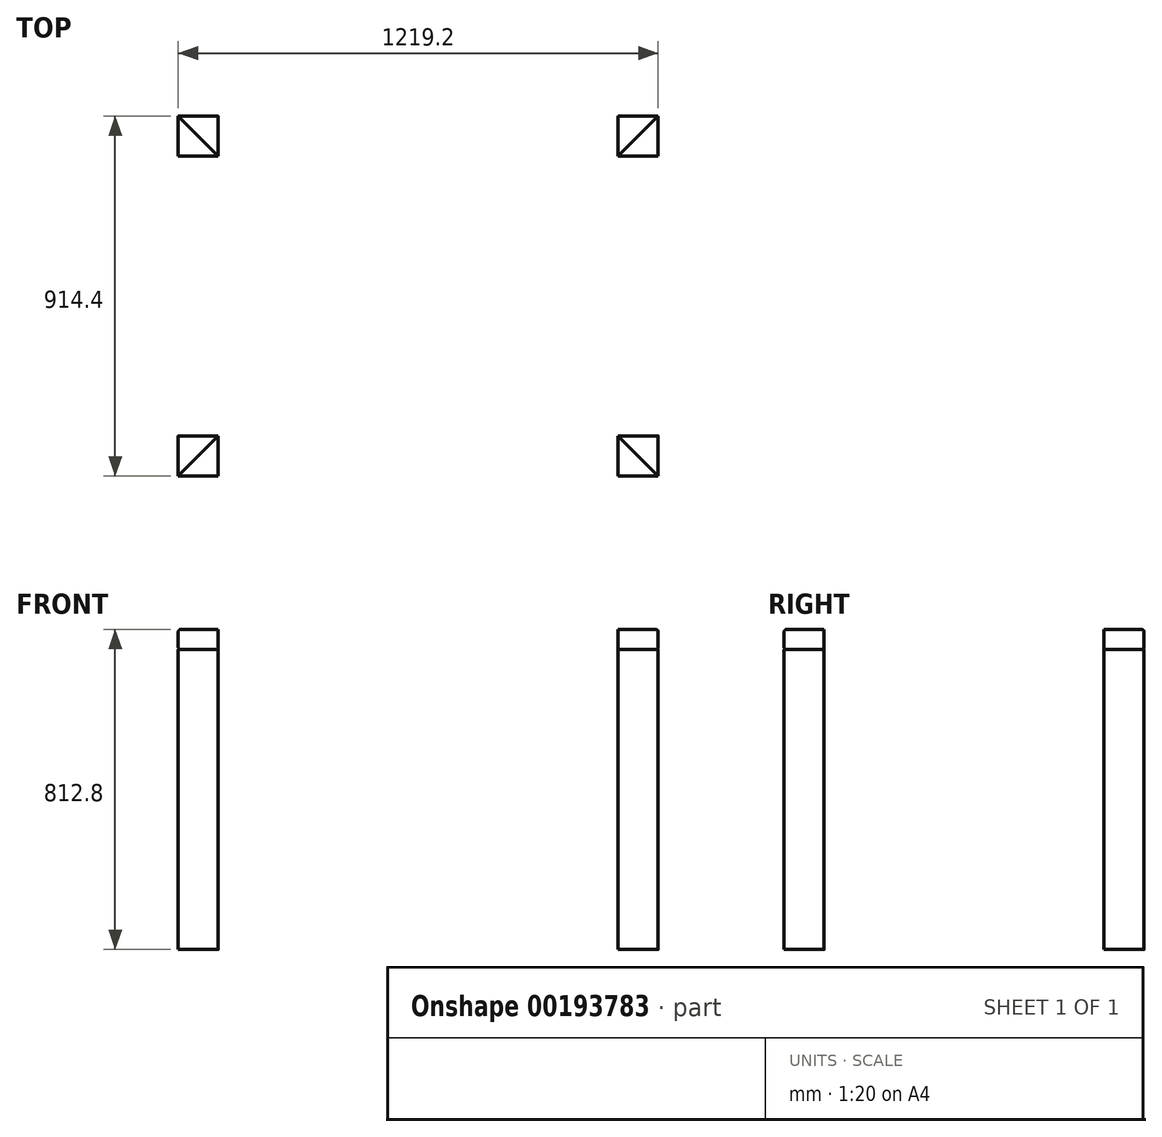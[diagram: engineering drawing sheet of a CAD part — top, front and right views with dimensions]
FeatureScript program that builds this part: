
annotation { "Feature Type Name" : "Feature", "Feature Type Description" : "" }
export const myFeature = defineFeature(function(context is Context, id is Id, definition is map)
    precondition{}
    {
        {
            var Q0;
            Q0=qCreatedBy(makeId("Top.planeOp"),FACE);
            var sketch = newSketch(context, id + "F0", { "sketchPlane" : qUnion([Q0])});
            skLineSegment(sketch, "E0.bottom", {"start": v(-609.6, 457.2) * mm, "end": v(609.6, 457.2) * mm});
            skLineSegment(sketch, "E0.top", {"start": v(-609.6, -457.2) * mm, "end": v(609.6, -457.2) * mm});
            skLineSegment(sketch, "E0.left", {"start": v(-609.6, 457.2) * mm, "end": v(-609.6, -457.2) * mm});
            skLineSegment(sketch, "E0.right", {"start": v(609.6, 457.2) * mm, "end": v(609.6, -457.2) * mm});
            skLineSegment(sketch, "E1.bottom", {"start": v(-508, 355.6) * mm, "end": v(508, 355.6) * mm});
            skLineSegment(sketch, "E1.top", {"start": v(-508, -355.6) * mm, "end": v(508, -355.6) * mm});
            skLineSegment(sketch, "E1.left", {"start": v(-508, 355.6) * mm, "end": v(-508, -355.6) * mm});
            skLineSegment(sketch, "E1.right", {"start": v(508, 355.6) * mm, "end": v(508, -355.6) * mm});
            skLineSegment(sketch, "E2", {"start": v(-609.6, 457.2) * mm, "end": v(-508, 355.6) * mm});
            skLineSegment(sketch, "E3", {"start": v(-609.6, -457.2) * mm, "end": v(-508, -355.6) * mm});
            skLineSegment(sketch, "E4", {"start": v(609.6, -457.2) * mm, "end": v(508, -355.6) * mm});
            skLineSegment(sketch, "E5", {"start": v(609.6, 457.2) * mm, "end": v(508, 355.6) * mm});
            skLineSegment(sketch, "E6.bottom", {"start": v(-609.6, 457.2) * mm, "end": v(-508, 457.2) * mm});
            skLineSegment(sketch, "E6.top", {"start": v(-609.6, 355.6) * mm, "end": v(-508, 355.6) * mm});
            skLineSegment(sketch, "E6.left", {"start": v(-609.6, 457.2) * mm, "end": v(-609.6, 355.6) * mm});
            skLineSegment(sketch, "E6.right", {"start": v(-508, 457.2) * mm, "end": v(-508, 355.6) * mm});
            skLineSegment(sketch, "E7.bottom", {"start": v(-609.6, -457.2) * mm, "end": v(-508, -457.2) * mm});
            skLineSegment(sketch, "E7.top", {"start": v(-609.6, -355.6) * mm, "end": v(-508, -355.6) * mm});
            skLineSegment(sketch, "E7.left", {"start": v(-609.6, -457.2) * mm, "end": v(-609.6, -355.6) * mm});
            skLineSegment(sketch, "E7.right", {"start": v(-508, -457.2) * mm, "end": v(-508, -355.6) * mm});
            skLineSegment(sketch, "E8.bottom", {"start": v(609.6, -457.2) * mm, "end": v(508, -457.2) * mm});
            skLineSegment(sketch, "E8.top", {"start": v(609.6, -355.6) * mm, "end": v(508, -355.6) * mm});
            skLineSegment(sketch, "E8.left", {"start": v(609.6, -457.2) * mm, "end": v(609.6, -355.6) * mm});
            skLineSegment(sketch, "E8.right", {"start": v(508, -457.2) * mm, "end": v(508, -355.6) * mm});
            skLineSegment(sketch, "E9.bottom", {"start": v(-750.07, 827.14) * mm, "end": v(-773.47, 827.14) * mm});
            skLineSegment(sketch, "E9.top", {"start": v(-750.07, 756.94) * mm, "end": v(-773.47, 756.94) * mm});
            skLineSegment(sketch, "E9.left", {"start": v(-750.07, 827.14) * mm, "end": v(-750.07, 756.94) * mm});
            skLineSegment(sketch, "E9.right", {"start": v(-773.47, 827.14) * mm, "end": v(-773.47, 756.94) * mm});
            skLineSegment(sketch, "E10.bottom", {"start": v(609.6, 457.2) * mm, "end": v(508, 457.2) * mm});
            skLineSegment(sketch, "E10.top", {"start": v(609.6, 355.6) * mm, "end": v(508, 355.6) * mm});
            skLineSegment(sketch, "E10.left", {"start": v(609.6, 457.2) * mm, "end": v(609.6, 355.6) * mm});
            skLineSegment(sketch, "E10.right", {"start": v(508, 457.2) * mm, "end": v(508, 355.6) * mm});
            skSolve(sketch);
        }
        {
            var Q0;
            Q0=makeQuery(id+"F0.imprint","IMPRINT",FACE,{"disambiguationData":[TD([[makeQuery(id+"F0.imprint","IMPRINT",EDGE,{"derivedFrom":sQuery(id+"F0.wireOp",EDGE,"E0.left")}),1.0]])]});
            var Q1;
            Q1=makeQuery(id+"F0.imprint","IMPRINT",FACE,{"disambiguationData":[TD([[makeQuery(id+"F0.imprint","IMPRINT",EDGE,{"derivedFrom":sQuery(id+"F0.wireOp",EDGE,"E2")}),-1.0]])]});
            var Q2;
            Q2=makeQuery(id+"F0.imprint","IMPRINT",FACE,{"disambiguationData":[TD([[makeQuery(id+"F0.imprint","IMPRINT",EDGE,{"derivedFrom":sQuery(id+"F0.wireOp",EDGE,"E3")}),1.0]])]});
            extrude(context, id + "F1", {"entities" : qUnion([Q0, Q1, Q2]), "depth" : 50.8 * mm});
        }
        {
            var Q0;
            Q0=makeQuery(id+"F0.imprint","IMPRINT",FACE,{"disambiguationData":[TD([[makeQuery(id+"F0.imprint","IMPRINT",EDGE,{"derivedFrom":sQuery(id+"F0.wireOp",EDGE,"E0.bottom")}),-1.0]])]});
            var Q1;
            Q1=makeQuery(id+"F0.imprint","IMPRINT",FACE,{"disambiguationData":[TD([[makeQuery(id+"F0.imprint","IMPRINT",EDGE,{"derivedFrom":sQuery(id+"F0.wireOp",EDGE,"E2")}),1.0]])]});
            var Q2;
            Q2=makeQuery(id+"F0.imprint","IMPRINT",FACE,{"disambiguationData":[TD([[makeQuery(id+"F0.imprint","IMPRINT",EDGE,{"derivedFrom":sQuery(id+"F0.wireOp",EDGE,"E5")}),-1.0]])]});
            extrude(context, id + "F2", {"entities" : qUnion([Q0, Q1, Q2]), "depth" : 50.8 * mm});
        }
        {
            var Q0;
            Q0=makeQuery(id+"F0.imprint","IMPRINT",FACE,{"disambiguationData":[TD([[makeQuery(id+"F0.imprint","IMPRINT",EDGE,{"derivedFrom":sQuery(id+"F0.wireOp",EDGE,"E0.right")}),-1.0]])]});
            var Q1;
            Q1=makeQuery(id+"F0.imprint","IMPRINT",FACE,{"disambiguationData":[TD([[makeQuery(id+"F0.imprint","IMPRINT",EDGE,{"derivedFrom":sQuery(id+"F0.wireOp",EDGE,"E4")}),-1.0]])]});
            var Q2;
            Q2=makeQuery(id+"F0.imprint","IMPRINT",FACE,{"disambiguationData":[TD([[makeQuery(id+"F0.imprint","IMPRINT",EDGE,{"derivedFrom":sQuery(id+"F0.wireOp",EDGE,"E5")}),1.0]])]});
            extrude(context, id + "F3", {"entities" : qUnion([Q0, Q1, Q2]), "depth" : 50.8 * mm});
        }
        {
            var Q0;
            Q0=makeQuery(id+"F0.imprint","IMPRINT",FACE,{"disambiguationData":[TD([[makeQuery(id+"F0.imprint","IMPRINT",EDGE,{"derivedFrom":sQuery(id+"F0.wireOp",EDGE,"E0.top")}),1.0]])]});
            var Q1;
            Q1=makeQuery(id+"F0.imprint","IMPRINT",FACE,{"disambiguationData":[TD([[makeQuery(id+"F0.imprint","IMPRINT",EDGE,{"derivedFrom":sQuery(id+"F0.wireOp",EDGE,"E4")}),1.0]])]});
            var Q2;
            Q2=makeQuery(id+"F0.imprint","IMPRINT",FACE,{"disambiguationData":[TD([[makeQuery(id+"F0.imprint","IMPRINT",EDGE,{"derivedFrom":sQuery(id+"F0.wireOp",EDGE,"E3")}),-1.0]])]});
            extrude(context, id + "F4", {"entities" : qUnion([Q0, Q1, Q2]), "depth" : 50.8 * mm});
        }
        {
            var Q0;
            Q0=makeQuery(id+"F4.opExtrude","CAP_EDGE",EDGE,{"disambiguationData":[OSD([sQuery(id+"F0.wireOp",EDGE,"E0.top"),sQuery(id+"F0.wireOp",EDGE,"E7.bottom"),sQuery(id+"F0.wireOp",EDGE,"E8.bottom")])],"isStart":false});
            var Q1;
            Q1=makeQuery(id+"F4.opExtrude","CAP_EDGE",EDGE,{"disambiguationData":[OSD([sQuery(id+"F0.wireOp",EDGE,"E0.top"),sQuery(id+"F0.wireOp",EDGE,"E7.bottom"),sQuery(id+"F0.wireOp",EDGE,"E8.bottom")])],"isStart":true});
            var Q2;
            Q2=makeQuery(id+"F4.opExtrude","CAP_EDGE",EDGE,{"disambiguationData":[OSD([sQuery(id+"F0.wireOp",EDGE,"E1.top")])],"isStart":false});
            var Q3;
            Q3=makeQuery(id+"F4.opExtrude","CAP_EDGE",EDGE,{"disambiguationData":[OSD([sQuery(id+"F0.wireOp",EDGE,"E1.top")])],"isStart":true});
            var Q4;
            Q4=makeQuery(id+"F3.opExtrude","CAP_EDGE",EDGE,{"disambiguationData":[OSD([sQuery(id+"F0.wireOp",EDGE,"E0.right"),sQuery(id+"F0.wireOp",EDGE,"E8.left"),sQuery(id+"F0.wireOp",EDGE,"E10.left")])],"isStart":true});
            var Q5;
            Q5=makeQuery(id+"F3.opExtrude","CAP_EDGE",EDGE,{"disambiguationData":[OSD([sQuery(id+"F0.wireOp",EDGE,"E0.right"),sQuery(id+"F0.wireOp",EDGE,"E8.left"),sQuery(id+"F0.wireOp",EDGE,"E10.left")])],"isStart":false});
            var Q6;
            Q6=makeQuery(id+"F3.opExtrude","CAP_EDGE",EDGE,{"disambiguationData":[OSD([sQuery(id+"F0.wireOp",EDGE,"E1.right")])],"isStart":false});
            var Q7;
            Q7=makeQuery(id+"F1.opExtrude","CAP_EDGE",EDGE,{"disambiguationData":[OSD([sQuery(id+"F0.wireOp",EDGE,"E1.left")])],"isStart":true});
            var Q8;
            Q8=makeQuery(id+"F1.opExtrude","CAP_EDGE",EDGE,{"disambiguationData":[OSD([sQuery(id+"F0.wireOp",EDGE,"E1.left")])],"isStart":false});
            var Q9;
            Q9=makeQuery(id+"F1.opExtrude","CAP_EDGE",EDGE,{"disambiguationData":[OSD([sQuery(id+"F0.wireOp",EDGE,"E0.left"),sQuery(id+"F0.wireOp",EDGE,"E6.left"),sQuery(id+"F0.wireOp",EDGE,"E7.left")])],"isStart":false});
            var Q10;
            Q10=makeQuery(id+"F2.opExtrude","CAP_EDGE",EDGE,{"disambiguationData":[OSD([sQuery(id+"F0.wireOp",EDGE,"E1.bottom")])],"isStart":false});
            var Q11;
            Q11=makeQuery(id+"F2.opExtrude","CAP_EDGE",EDGE,{"disambiguationData":[OSD([sQuery(id+"F0.wireOp",EDGE,"E0.bottom"),sQuery(id+"F0.wireOp",EDGE,"E6.bottom"),sQuery(id+"F0.wireOp",EDGE,"E10.bottom")])],"isStart":false});
            var Q12;
            Q12=makeQuery(id+"F2.opExtrude","CAP_EDGE",EDGE,{"disambiguationData":[OSD([sQuery(id+"F0.wireOp",EDGE,"E0.bottom"),sQuery(id+"F0.wireOp",EDGE,"E6.bottom"),sQuery(id+"F0.wireOp",EDGE,"E10.bottom")])],"isStart":true});
            var Q13;
            Q13=makeQuery(id+"F2.opExtrude","CAP_EDGE",EDGE,{"disambiguationData":[OSD([sQuery(id+"F0.wireOp",EDGE,"E1.bottom")])],"isStart":true});
            var Q14;
            Q14=makeQuery(id+"F1.opExtrude","CAP_EDGE",EDGE,{"disambiguationData":[OSD([sQuery(id+"F0.wireOp",EDGE,"E0.left"),sQuery(id+"F0.wireOp",EDGE,"E6.left"),sQuery(id+"F0.wireOp",EDGE,"E7.left")])],"isStart":true});
            var Q15;
            Q15=makeQuery(id+"F3.opExtrude","CAP_EDGE",EDGE,{"disambiguationData":[OSD([sQuery(id+"F0.wireOp",EDGE,"E1.right")])],"isStart":true});
            fillet(context, id + "F5", {"entities" : qUnion([Q0, Q1, Q2, Q3, Q4, Q5, Q6, Q7, Q8, Q9, Q10, Q11, Q12, Q13, Q14, Q15]), "radius" : 6.35 * mm, "tangentPropagation" : true, "allowEdgeOverflow" : false});
        }
        {
            var Q0;
            Q0=makeQuery(id+"F0.imprint","IMPRINT",FACE,{"disambiguationData":[TD([[makeQuery(id+"F0.imprint","IMPRINT",EDGE,{"derivedFrom":sQuery(id+"F0.wireOp",EDGE,"E2")}),1.0]])]});
            var Q1;
            Q1=makeQuery(id+"F0.imprint","IMPRINT",FACE,{"disambiguationData":[TD([[makeQuery(id+"F0.imprint","IMPRINT",EDGE,{"derivedFrom":sQuery(id+"F0.wireOp",EDGE,"E2")}),-1.0]])]});
            extrude(context, id + "F6", {"entities" : qUnion([Q0, Q1]), "oppositeDirection" : true, "depth" : 762 * mm});
        }
        {
            var Q0;
            Q0=makeQuery(id+"F0.imprint","IMPRINT",FACE,{"disambiguationData":[TD([[makeQuery(id+"F0.imprint","IMPRINT",EDGE,{"derivedFrom":sQuery(id+"F0.wireOp",EDGE,"E3")}),1.0]])]});
            var Q1;
            Q1=makeQuery(id+"F0.imprint","IMPRINT",FACE,{"disambiguationData":[TD([[makeQuery(id+"F0.imprint","IMPRINT",EDGE,{"derivedFrom":sQuery(id+"F0.wireOp",EDGE,"E3")}),-1.0]])]});
            extrude(context, id + "F7", {"entities" : qUnion([Q0, Q1]), "oppositeDirection" : true, "depth" : 762 * mm});
        }
        {
            var Q0;
            Q0=makeQuery(id+"F0.imprint","IMPRINT",FACE,{"disambiguationData":[TD([[makeQuery(id+"F0.imprint","IMPRINT",EDGE,{"derivedFrom":sQuery(id+"F0.wireOp",EDGE,"E5")}),1.0]])]});
            var Q1;
            Q1=makeQuery(id+"F0.imprint","IMPRINT",FACE,{"disambiguationData":[TD([[makeQuery(id+"F0.imprint","IMPRINT",EDGE,{"derivedFrom":sQuery(id+"F0.wireOp",EDGE,"E5")}),-1.0]])]});
            extrude(context, id + "F8", {"entities" : qUnion([Q0, Q1]), "oppositeDirection" : true, "depth" : 762 * mm});
        }
        {
            var Q0;
            Q0=makeQuery(id+"F0.imprint","IMPRINT",FACE,{"disambiguationData":[TD([[makeQuery(id+"F0.imprint","IMPRINT",EDGE,{"derivedFrom":sQuery(id+"F0.wireOp",EDGE,"E4")}),1.0]])]});
            var Q1;
            Q1=makeQuery(id+"F0.imprint","IMPRINT",FACE,{"disambiguationData":[TD([[makeQuery(id+"F0.imprint","IMPRINT",EDGE,{"derivedFrom":sQuery(id+"F0.wireOp",EDGE,"E4")}),-1.0]])]});
            extrude(context, id + "F9", {"entities" : qUnion([Q0, Q1]), "oppositeDirection" : true, "depth" : 762 * mm});
        }
        {
            var Q0;
            Q0=makeQuery(id+"F9.opExtrude","SWEPT_EDGE",EDGE,{"disambiguationData":[OSD([sQuery(id+"F0.wireOp",EDGE,"E4"),sQuery(id+"F0.wireOp",EDGE,"E8.bottom"),sQuery(id+"F0.wireOp",EDGE,"E8.left")])]});
            var Q1;
            Q1=makeQuery(id+"F9.opExtrude","SWEPT_EDGE",EDGE,{"disambiguationData":[OSD([sQuery(id+"F0.wireOp",EDGE,"E0.top"),sQuery(id+"F0.wireOp",EDGE,"E8.bottom"),sQuery(id+"F0.wireOp",EDGE,"E8.right")])]});
            var Q2;
            Q2=makeQuery(id+"F9.opExtrude","SWEPT_EDGE",EDGE,{"disambiguationData":[OSD([sQuery(id+"F0.wireOp",EDGE,"E0.right"),sQuery(id+"F0.wireOp",EDGE,"E8.top"),sQuery(id+"F0.wireOp",EDGE,"E8.left")])]});
            var Q3;
            Q3=makeQuery(id+"F7.opExtrude","SWEPT_EDGE",EDGE,{"disambiguationData":[OSD([sQuery(id+"F0.wireOp",EDGE,"E1.top"),sQuery(id+"F0.wireOp",EDGE,"E1.left"),sQuery(id+"F0.wireOp",EDGE,"E3"),sQuery(id+"F0.wireOp",EDGE,"E7.top"),sQuery(id+"F0.wireOp",EDGE,"E7.right")])]});
            var Q4;
            Q4=makeQuery(id+"F7.opExtrude","SWEPT_EDGE",EDGE,{"disambiguationData":[OSD([sQuery(id+"F0.wireOp",EDGE,"E0.top"),sQuery(id+"F0.wireOp",EDGE,"E7.bottom"),sQuery(id+"F0.wireOp",EDGE,"E7.right")])]});
            var Q5;
            Q5=makeQuery(id+"F7.opExtrude","SWEPT_EDGE",EDGE,{"disambiguationData":[OSD([sQuery(id+"F0.wireOp",EDGE,"E3"),sQuery(id+"F0.wireOp",EDGE,"E7.bottom"),sQuery(id+"F0.wireOp",EDGE,"E7.left")])]});
            var Q6;
            Q6=makeQuery(id+"F6.opExtrude","SWEPT_EDGE",EDGE,{"disambiguationData":[OSD([sQuery(id+"F0.wireOp",EDGE,"E0.left"),sQuery(id+"F0.wireOp",EDGE,"E6.top"),sQuery(id+"F0.wireOp",EDGE,"E6.left")])]});
            var Q7;
            Q7=makeQuery(id+"F6.opExtrude","SWEPT_EDGE",EDGE,{"disambiguationData":[OSD([sQuery(id+"F0.wireOp",EDGE,"E1.bottom"),sQuery(id+"F0.wireOp",EDGE,"E1.left"),sQuery(id+"F0.wireOp",EDGE,"E2"),sQuery(id+"F0.wireOp",EDGE,"E6.top"),sQuery(id+"F0.wireOp",EDGE,"E6.right")])]});
            var Q8;
            Q8=makeQuery(id+"F6.opExtrude","SWEPT_EDGE",EDGE,{"disambiguationData":[OSD([sQuery(id+"F0.wireOp",EDGE,"E0.bottom"),sQuery(id+"F0.wireOp",EDGE,"E6.bottom"),sQuery(id+"F0.wireOp",EDGE,"E6.right")])]});
            var Q9;
            Q9=makeQuery(id+"F8.opExtrude","SWEPT_EDGE",EDGE,{"disambiguationData":[OSD([sQuery(id+"F0.wireOp",EDGE,"E1.bottom"),sQuery(id+"F0.wireOp",EDGE,"E1.right"),sQuery(id+"F0.wireOp",EDGE,"E5"),sQuery(id+"F0.wireOp",EDGE,"E10.top"),sQuery(id+"F0.wireOp",EDGE,"E10.right")])]});
            var Q10;
            Q10=makeQuery(id+"F8.opExtrude","SWEPT_EDGE",EDGE,{"disambiguationData":[OSD([sQuery(id+"F0.wireOp",EDGE,"E0.right"),sQuery(id+"F0.wireOp",EDGE,"E10.top"),sQuery(id+"F0.wireOp",EDGE,"E10.left")])]});
            var Q11;
            Q11=makeQuery(id+"F8.opExtrude","SWEPT_EDGE",EDGE,{"disambiguationData":[OSD([sQuery(id+"F0.wireOp",EDGE,"E5"),sQuery(id+"F0.wireOp",EDGE,"E10.bottom"),sQuery(id+"F0.wireOp",EDGE,"E10.left")])]});
            var Q12;
            Q12=makeQuery(id+"F8.opExtrude","SWEPT_EDGE",EDGE,{"disambiguationData":[OSD([sQuery(id+"F0.wireOp",EDGE,"E0.bottom"),sQuery(id+"F0.wireOp",EDGE,"E10.bottom"),sQuery(id+"F0.wireOp",EDGE,"E10.right")])]});
            var Q13;
            Q13=makeQuery(id+"F9.opExtrude","SWEPT_EDGE",EDGE,{"disambiguationData":[OSD([sQuery(id+"F0.wireOp",EDGE,"E1.top"),sQuery(id+"F0.wireOp",EDGE,"E1.right"),sQuery(id+"F0.wireOp",EDGE,"E4"),sQuery(id+"F0.wireOp",EDGE,"E8.top"),sQuery(id+"F0.wireOp",EDGE,"E8.right")])]});
            var Q14;
            Q14=makeQuery(id+"F6.opExtrude","SWEPT_EDGE",EDGE,{"disambiguationData":[OSD([sQuery(id+"F0.wireOp",EDGE,"E2"),sQuery(id+"F0.wireOp",EDGE,"E6.bottom"),sQuery(id+"F0.wireOp",EDGE,"E6.left")])]});
            var Q15;
            Q15=makeQuery(id+"F7.opExtrude","SWEPT_EDGE",EDGE,{"disambiguationData":[OSD([sQuery(id+"F0.wireOp",EDGE,"E0.left"),sQuery(id+"F0.wireOp",EDGE,"E7.top"),sQuery(id+"F0.wireOp",EDGE,"E7.left")])]});
            fillet(context, id + "F10", {"entities" : qUnion([Q0, Q1, Q2, Q3, Q4, Q5, Q6, Q7, Q8, Q9, Q10, Q11, Q12, Q13, Q14, Q15]), "radius" : 6.35 * mm, "tangentPropagation" : true, "allowEdgeOverflow" : false});
        }
    });
